# Revit family: CWW
name_source: partatom
category: Lighting Fixtures
revit_build: Autodesk Revit MEP 2012 (Build: 20110309_2315(x64)
units: mm (PartAtom-declared; Revit-internal decimal feet)

## types (6) — shared parameters
Ceiling Type = Grid
Color Filter = 16777215
Default Elevation = 4' - 0"
Description = Contemporary LED Wall Wash
Dimming Lamp Color Temperature Shift = <None>
Emit Shape Visible in Rendering = No
Emit from Rectangle Width = 0' - 3 1/2"
Lamp = LED Lamp
Load Classification = Lighting
Manufacturer = Columbia Lighting
Manufacturer Fax = 866-898-1065
Material Finish = Hubbell - Paint - White
Model = CWW
Opal lens = Hubbell - Glass
Photometric Web Link = http://www.columbialighting.com
Photometric Web Notes = More IES files Download Photometric Web Link
Power Factor = 1
Product Documentation Link = http://cdn.columbialighting.com
Product Page URL = http://www.columbialighting.com
Technical Support = 864-678-1000
Tilt Angle = -90.00°
URL = http://www.columbialighting.com
Voltage = 120 V
Warranty = Five year warranty
Wattage Comments = 20W-23.2W

## per-type parameters (varying)
| type | Apparent Load | Distribution | Emit from Rectangle Length | Length | Lumen Output | Photometric Web File | Watts |
| CWW4-40XWG-2WW-EDU | 25 VA | Double Wallwash | 3' - 10" | 4' - 0" | Extra Low Watt | CWW4-40XWG-2WW-EDU.ies | 25 W |
| CWW4-50MLG-1WW-EDU | 50 VA | Asymmetric Wallwash | 3' - 10" | 4' - 0" | Medium Lumen | CWW4-50MLG-1WW-EDU.ies | 50 W |
| CWW4-50XWG-1WR-EDU | 25 VA | Asymmetric Wallwash with Roomside | 3' - 10" | 4' - 0" | Extra Low Watt | CWW4-50XWG-1WR-EDU.ies | 25 W |
| CWW2-30VWG-2WW-EDU | 15 VA | Double Wallwash | 1' - 10" | 2' - 0" | Very Low Watt | CWW2-30VWG-2WW-EDU.ies | 15 W |
| CWW2-30MWG-1WW-EDU | 20 VA | Asymmetric Wallwash | 1' - 10" | 2' - 0" | Medium Low Watt | CWW2-30MWG-1WW-EDU.ies | 20 W |
| CWW2-30LWG-1WR-EDU | 27 VA | Asymmetric Wallwash with Roomside | 1' - 10" | 2' - 0" | Low Watt | 2x4 2Lamp.ies | 27 W |

## geometry (parser evidence)
native form markers: Sweep x6
no freeform markers — native parametric forms only
